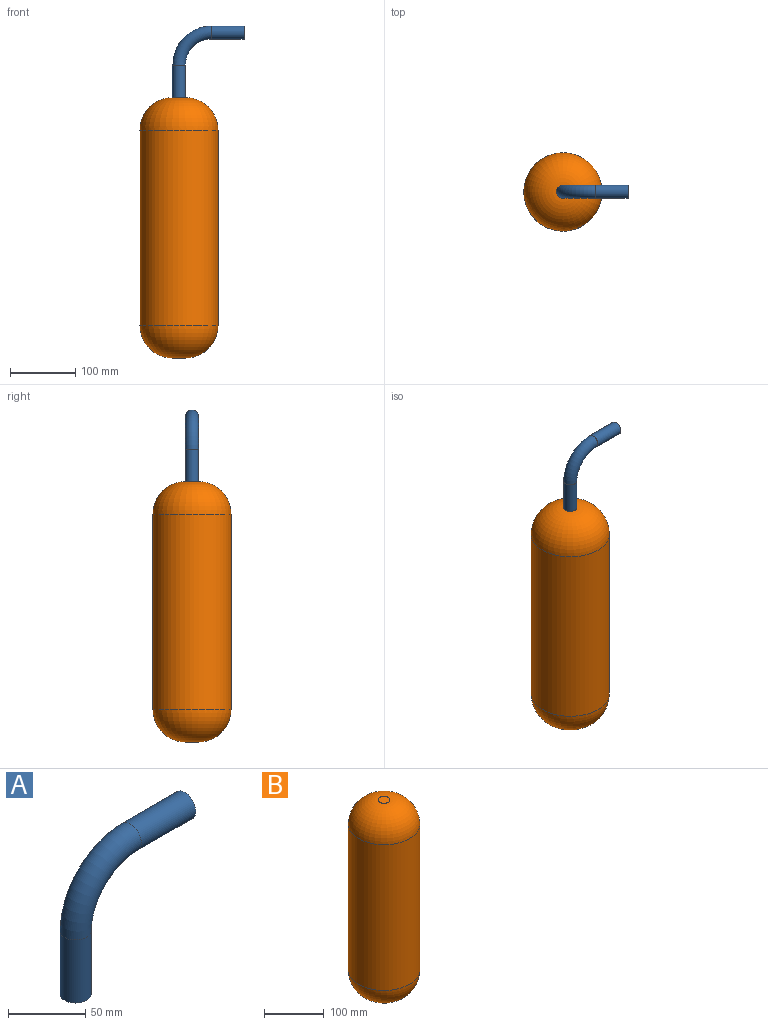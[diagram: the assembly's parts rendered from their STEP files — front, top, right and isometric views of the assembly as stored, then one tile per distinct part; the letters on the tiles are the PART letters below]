
ASSEMBLY  parts=2 mates=1
PART A: 5 faces, bbox 114.9x20x114.9 mm
  f0: plane 20x20mm, normal (0,0,-1), area 314.2mm2, adj f2
  f1: plane 20x20mm, normal (1,0,0), area 314.2mm2, adj f4
  f2: cylinder r=10mm len=50mm, axis (0,0,1), area 3141.6mm2, adj f0,f3
  f3: torus R=50mm, axis (0,1,0), area 4934.8mm2, adj f2,f4
  f4: cylinder r=10mm len=50mm, axis (1,0,0), area 3141.6mm2, adj f1,f3
PART B: 5 faces, bbox 120x120x400 mm
  f0: cylinder r=60mm len=300mm, axis (0,0,-1), area 113097.3mm2, adj f3,f4
  f1: plane 20x20mm, normal (0,0,1), area 314.2mm2, adj f4
  f2: plane 20x20mm, normal (0,0,-1), area 314.2mm2, adj f3
  f3: torus R=10mm, axis (0,0,1), area 20642.8mm2, adj f0,f2
  f4: torus R=10mm, axis (0,0,1), area 20642.8mm2, adj f0,f1
PLACE A t=(-89.95,154.26,92.32)mm
PLACE B t=(-89.95,154.26,-307.68)mm
MATE revolute B.f0 <-> A.f2  axis (0,0,1) through (-89.95,154.26,92.32)mm
